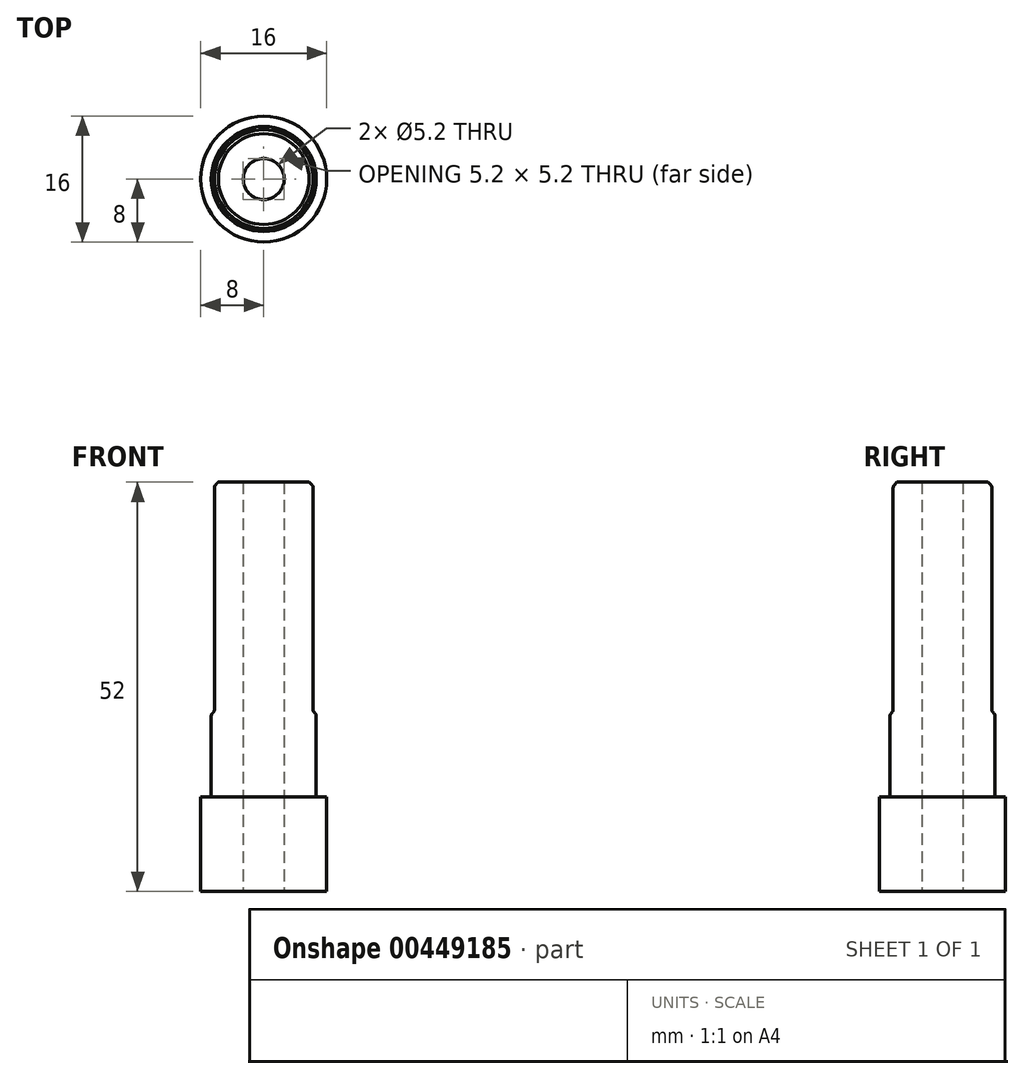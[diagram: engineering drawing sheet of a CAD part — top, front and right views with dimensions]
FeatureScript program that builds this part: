
annotation { "Feature Type Name" : "Feature", "Feature Type Description" : "" }
export const myFeature = defineFeature(function(context is Context, id is Id, definition is map)
    precondition{}
    {
        {
            var Q0;
            Q0=qCreatedBy(makeId("Top.planeOp"),FACE);
            var sketch = newSketch(context, id + "F0", { "sketchPlane" : qUnion([Q0])});
            skCircle(sketch, "E0", {"center": v(0, 0) * mm, "radius": 6.67 * mm});
            skCircle(sketch, "E1", {"center": v(0, 0) * mm, "radius": 6.26 * mm});
            skCircle(sketch, "E2", {"center": v(0, 0) * mm, "radius": 8 * mm});
            skSolve(sketch);
        }
        {
            var Q0;
            Q0=makeQuery(id+"F0.imprint","IMPRINT",FACE,{"disambiguationData":[TD([[makeQuery(id+"F0.imprint","IMPRINT",EDGE,{"derivedFrom":sQuery(id+"F0.wireOp",EDGE,"E1")}),1.0]])]});
            var Q1;
            Q1=makeQuery(id+"F0.imprint","IMPRINT",FACE,{"disambiguationData":[TD([[makeQuery(id+"F0.imprint","IMPRINT",EDGE,{"derivedFrom":sQuery(id+"F0.wireOp",EDGE,"E0")}),1.0]])]});
            extrude(context, id + "F1", {"entities" : qUnion([Q0, Q1]), "depth" : 11 * mm});
        }
        {
            var Q0;
            Q0=makeQuery(id+"F0.imprint","IMPRINT",FACE,{"disambiguationData":[TD([[makeQuery(id+"F0.imprint","IMPRINT",EDGE,{"derivedFrom":sQuery(id+"F0.wireOp",EDGE,"E1")}),1.0]])]});
            extrude(context, id + "F2", {"entities" : qUnion([Q0]), "operationType" : NewBodyOperationType.ADD, "depth" : 40 * mm});
        }
        {
            var Q0;
            Q0=makeQuery(id+"F0.imprint","IMPRINT",FACE,{"disambiguationData":[TD([[makeQuery(id+"F0.imprint","IMPRINT",EDGE,{"derivedFrom":sQuery(id+"F0.wireOp",EDGE,"E1")}),1.0]])]});
            var Q1;
            Q1=makeQuery(id+"F0.imprint","IMPRINT",FACE,{"disambiguationData":[TD([[makeQuery(id+"F0.imprint","IMPRINT",EDGE,{"derivedFrom":sQuery(id+"F0.wireOp",EDGE,"E0")}),1.0]])]});
            var Q2;
            Q2=makeQuery(id+"F0.imprint","IMPRINT",FACE,{"disambiguationData":[TD([[makeQuery(id+"F0.imprint","IMPRINT",EDGE,{"derivedFrom":sQuery(id+"F0.wireOp",EDGE,"E0")}),-1.0]])]});
            extrude(context, id + "F3", {"entities" : qUnion([Q0, Q1, Q2]), "oppositeDirection" : true, "depth" : 12 * mm});
        }
        {
            var Q0;
            Q0=makeQuery(id+"F3.opExtrude","CAP_FACE",FACE,{"disambiguationData":[OSD([sQuery(id+"F0.wireOp",EDGE,"E2")])],"isStart":false});
            var sketch = newSketch(context, id + "F4", { "sketchPlane" : qUnion([Q0])});
            skCircle(sketch, "E3", {"center": v(0, 0) * mm, "radius": 2.6 * mm});
            skSolve(sketch);
        }
        {
            var Q0;
            Q0=makeQuery(id+"F4.imprint","IMPRINT",FACE,{"disambiguationData":[TD([[makeQuery(id+"F4.imprint","IMPRINT",EDGE,{"derivedFrom":sQuery(id+"F4.wireOp",EDGE,"E3")}),1.0]])]});
            extrude(context, id + "F5", {"entities" : qUnion([Q0]), "operationType" : NewBodyOperationType.REMOVE, "oppositeDirection" : true, "depth" : 52 * mm});
        }
        {
            var Q0;
            Q0=makeQuery(id+"F1.opExtrude","CAP_EDGE",EDGE,{"disambiguationData":[OSD([sQuery(id+"F0.wireOp",EDGE,"E0")])],"isStart":false});
            var Q1;
            Q1=makeQuery(id+"F2.opExtrude","CAP_EDGE",EDGE,{"disambiguationData":[OSD([sQuery(id+"F0.wireOp",EDGE,"E1")])],"isStart":false});
            var Q2;
            Q2=makeQuery(id+"F5.boolean.opBoolean","COPY",EDGE,{"derivedFrom":makeQuery(id+"F5.opExtrude","CAP_EDGE",EDGE,{"disambiguationData":[OSD([sQuery(id+"F4.wireOp",EDGE,"E3")])],"isStart":false})});
            var Q3;
            Q3=makeQuery(id+"F5.boolean.opBoolean","COPY",EDGE,{"derivedFrom":makeQuery(id+"F5.opExtrude","CAP_EDGE",EDGE,{"disambiguationData":[OSD([sQuery(id+"F4.wireOp",EDGE,"E3")])],"isStart":true})});
            chamfer(context, id + "F6", {"entities" : qUnion([Q0, Q1, Q2, Q3]), "width" : .5 * mm, "tangentPropagation" : true});
        }
        {
            var Q0;
            {var subQ0=sQuery(id+"F0.wireOp",EDGE,"E0");Q0=makeQuery(id+"F6.opChamfer","BLEND_EDGE",EDGE,{"blendedFrom":[makeQuery(id+"F1.opExtrude","CAP_EDGE",EDGE,{"disambiguationData":[OSD([subQ0])],"isStart":false}),makeQuery(id+"F1.opExtrude","SWEPT_FACE",FACE,{"disambiguationData":[OSD([subQ0])]})],"blendedInto":[makeQuery(id+"F1.opExtrude","SWEPT_FACE",FACE,{"disambiguationData":[OSD([subQ0])]})]});}
            var Q1;
            {var subQ0=sQuery(id+"F0.wireOp",EDGE,"E1");Q1=makeQuery(id+"F6.opChamfer","BLEND_EDGE",EDGE,{"blendedFrom":[makeQuery(id+"F2.opExtrude","CAP_EDGE",EDGE,{"disambiguationData":[OSD([subQ0])],"isStart":false}),makeQuery(id+"F2.opExtrude","SWEPT_FACE",FACE,{"disambiguationData":[OSD([subQ0])]})],"blendedInto":[makeQuery(id+"F2.opExtrude","SWEPT_FACE",FACE,{"disambiguationData":[OSD([subQ0])]})]});}
            var Q2;
            {var subQ0=sQuery(id+"F4.wireOp",EDGE,"E3");Q2=makeQuery(id+"F6.opChamfer","BLEND_EDGE",EDGE,{"blendedFrom":[makeQuery(id+"F5.boolean.opBoolean","COPY",EDGE,{"derivedFrom":makeQuery(id+"F5.opExtrude","CAP_EDGE",EDGE,{"disambiguationData":[OSD([subQ0])],"isStart":false})}),makeQuery(id+"F5.boolean.opBoolean","COPY",FACE,{"disambiguationData":[TD([makeQuery(id+"F1.opExtrude","CAP_FACE",FACE,{"disambiguationData":[OSD([sQuery(id+"F0.wireOp",EDGE,"E0")])],"isStart":true})])],"derivedFrom":makeQuery(id+"F5.opExtrude","SWEPT_FACE",FACE,{"disambiguationData":[OSD([subQ0])]})})],"blendedInto":[makeQuery(id+"F5.boolean.opBoolean","COPY",FACE,{"disambiguationData":[TD([makeQuery(id+"F1.opExtrude","CAP_FACE",FACE,{"disambiguationData":[OSD([sQuery(id+"F0.wireOp",EDGE,"E0")])],"isStart":true})])],"derivedFrom":makeQuery(id+"F5.opExtrude","SWEPT_FACE",FACE,{"disambiguationData":[OSD([subQ0])]})})]});}
            var Q3;
            {var subQ0=sQuery(id+"F0.wireOp",EDGE,"E2");var subQ1=sQuery(id+"F4.wireOp",EDGE,"E3");Q3=makeQuery(id+"F6.opChamfer","BLEND_EDGE",EDGE,{"blendedFrom":[makeQuery(id+"F5.boolean.opBoolean","COPY",EDGE,{"derivedFrom":makeQuery(id+"F5.opExtrude","CAP_EDGE",EDGE,{"disambiguationData":[OSD([subQ1])],"isStart":true})}),makeQuery(id+"F5.boolean.opBoolean","COPY",FACE,{"disambiguationData":[TD([makeQuery(id+"F3.opExtrude","CAP_FACE",FACE,{"disambiguationData":[OSD([subQ0])],"isStart":true})])],"derivedFrom":makeQuery(id+"F5.opExtrude","SWEPT_FACE",FACE,{"disambiguationData":[OSD([subQ1])]})})],"blendedInto":[makeQuery(id+"F5.boolean.opBoolean","COPY",FACE,{"disambiguationData":[TD([makeQuery(id+"F3.opExtrude","CAP_FACE",FACE,{"disambiguationData":[OSD([subQ0])],"isStart":true})])],"derivedFrom":makeQuery(id+"F5.opExtrude","SWEPT_FACE",FACE,{"disambiguationData":[OSD([subQ1])]})})]});}
            fillet(context, id + "F7", {"entities" : qUnion([Q0, Q1, Q2, Q3]), "radius" : .5 * mm, "tangentPropagation" : true, "allowEdgeOverflow" : false});
        }
        {
            var Q0;
            Q0=makeQuery(id+"F6.opChamfer","BLEND_EDGE",EDGE,{"blendedFrom":[makeQuery(id+"F1.opExtrude","CAP_EDGE",EDGE,{"disambiguationData":[OSD([sQuery(id+"F0.wireOp",EDGE,"E0")])],"isStart":false}),makeQuery(id+"F2.opExtrude","SWEPT_FACE",FACE,{"disambiguationData":[OSD([sQuery(id+"F0.wireOp",EDGE,"E1")])]})],"blendedInto":[makeQuery(id+"F2.opExtrude","SWEPT_FACE",FACE,{"disambiguationData":[OSD([sQuery(id+"F0.wireOp",EDGE,"E1")])]})]});
            fillet(context, id + "F8", {"entities" : qUnion([Q0]), "radius" : .5 * mm, "tangentPropagation" : true, "allowEdgeOverflow" : false});
        }
    });
